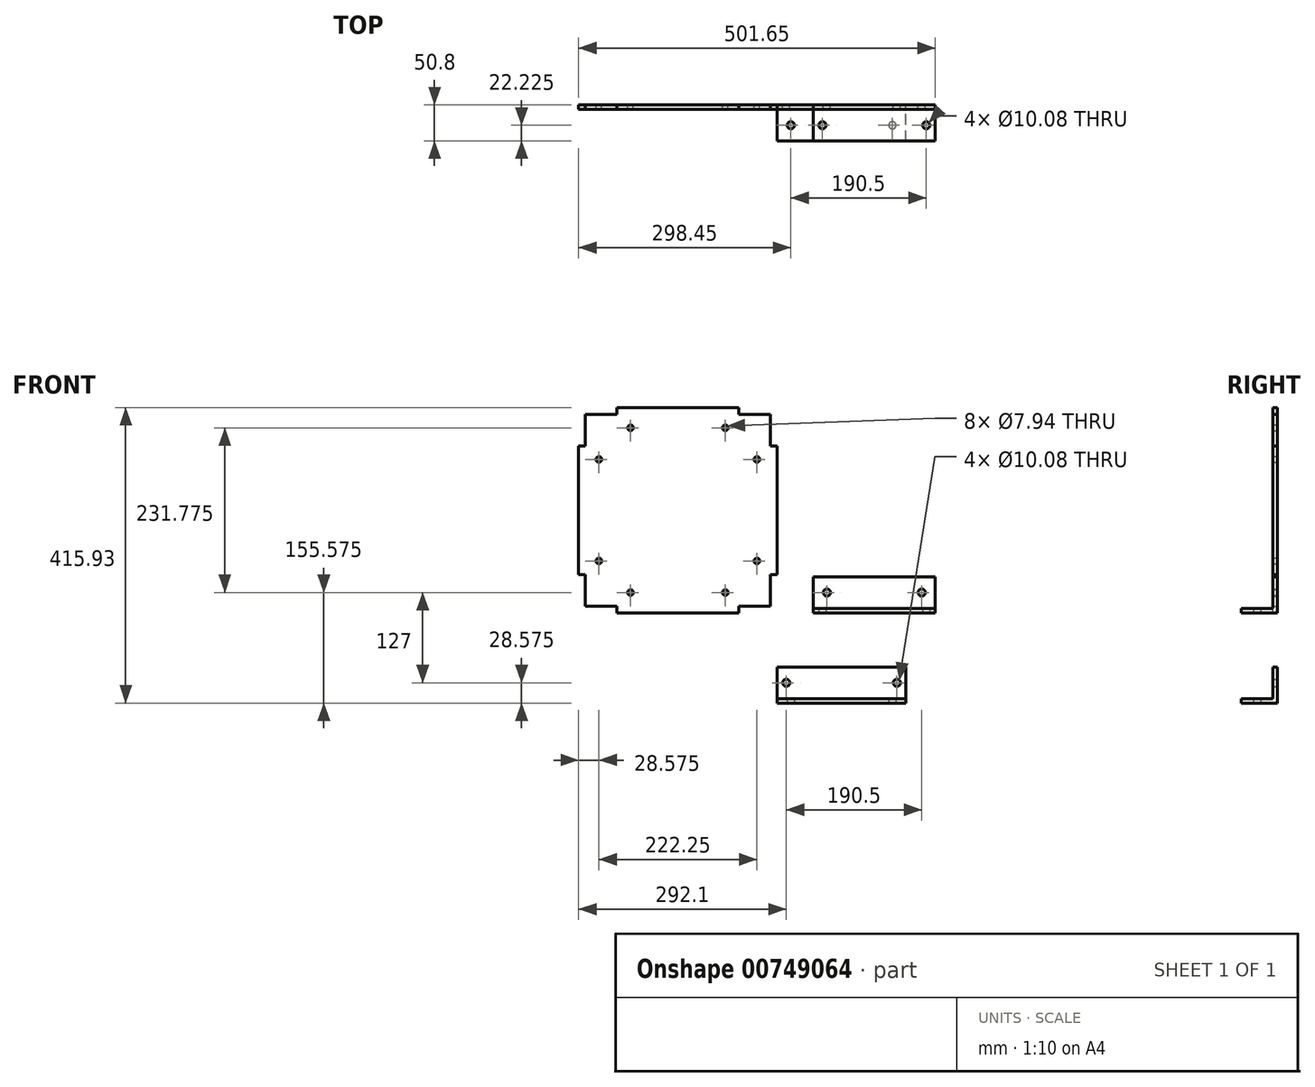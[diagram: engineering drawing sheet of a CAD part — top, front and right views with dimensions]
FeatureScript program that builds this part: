
annotation { "Feature Type Name" : "Feature", "Feature Type Description" : "" }
export const myFeature = defineFeature(function(context is Context, id is Id, definition is map)
    precondition{}
    {
        {
            var Q0;
            Q0=qCreatedBy(makeId("Front.planeOp"),FACE);
            var sketch = newSketch(context, id + "F0", { "sketchPlane" : qUnion([Q0])});
            skLineSegment(sketch, "E0.bottom", {"start": v(-53.98, 0) * mm, "end": v(-225.42, 0) * mm});
            skLineSegment(sketch, "E0.top", {"start": v(-53.98, 288.93) * mm, "end": v(-225.42, 288.93) * mm});
            skLineSegment(sketch, "E0.left", {"start": v(0, 53.98) * mm, "end": v(0, 234.95) * mm});
            skLineSegment(sketch, "E0.right", {"start": v(-279.4, 53.97) * mm, "end": v(-279.4, 234.95) * mm});
            skLineSegment(sketch, "E1", {"start": v(-139.7, 288.93) * mm, "end": v(-139.7, 0) * mm, "construction": true});
            skLineSegment(sketch, "E2", {"start": v(-279.4, 144.46) * mm, "end": v(0, 144.46) * mm, "construction": true});
            skLineSegment(sketch, "E3.top", {"start": v(-279.4, 234.95) * mm, "end": v(-269.88, 234.95) * mm});
            skLineSegment(sketch, "E3.right", {"start": v(-269.88, 279.4) * mm, "end": v(-269.88, 234.95) * mm});
            skLineSegment(sketch, "E4.top", {"start": v(-225.42, 279.4) * mm, "end": v(-269.88, 279.4) * mm});
            skLineSegment(sketch, "E4.left", {"start": v(-225.42, 288.93) * mm, "end": v(-225.42, 279.4) * mm});
            skPoint(sketch, "E5.orphan", {"position": v(-279.4, 288.93) * mm});
            skLineSegment(sketch, "E6.MirrorCS", {"start": v(-53.98, 288.93) * mm, "end": v(-53.98, 279.4) * mm});
            skLineSegment(sketch, "E7.MirrorCS", {"start": v(-53.98, 279.4) * mm, "end": v(-9.53, 279.4) * mm});
            skLineSegment(sketch, "E8.MirrorCS", {"start": v(-9.53, 279.4) * mm, "end": v(-9.53, 234.95) * mm});
            skLineSegment(sketch, "E9.MirrorCS", {"start": v(0, 234.95) * mm, "end": v(-9.53, 234.95) * mm});
            skLineSegment(sketch, "E10.MirrorCS", {"start": v(-53.98, 9.53) * mm, "end": v(-9.53, 9.53) * mm});
            skLineSegment(sketch, "E11.MirrorCS", {"start": v(-53.98, 0) * mm, "end": v(-53.98, 9.53) * mm});
            skLineSegment(sketch, "E12.MirrorCS", {"start": v(0, 53.97) * mm, "end": v(-9.53, 53.97) * mm});
            skLineSegment(sketch, "E13.MirrorCS", {"start": v(-9.53, 9.53) * mm, "end": v(-9.53, 53.97) * mm});
            skLineSegment(sketch, "E14.MirrorCS", {"start": v(-279.4, 53.97) * mm, "end": v(-269.88, 53.97) * mm});
            skLineSegment(sketch, "E15.MirrorCS", {"start": v(-269.88, 9.53) * mm, "end": v(-269.88, 53.97) * mm});
            skLineSegment(sketch, "E16.MirrorCS", {"start": v(-225.42, 9.53) * mm, "end": v(-269.88, 9.53) * mm});
            skLineSegment(sketch, "E17.MirrorCS", {"start": v(-225.42, 0) * mm, "end": v(-225.42, 9.53) * mm});
            skPoint(sketch, "E18.orphan", {"position": v(-279.4, 0) * mm});
            skPoint(sketch, "E19.orphan", {"position": v(0, 0) * mm});
            skPoint(sketch, "E20.orphan", {"position": v(0, 288.92) * mm});
            skSolve(sketch);
        }
        {
            var Q0;
            Q0 = qSketchRegion(id + "F0", true);
            extrude(context, id + "F1", {"entities" : qUnion([Q0]), "depth" : 6.35 * mm, "offsetDistance" : 25.4 * mm});
        }
        {
            var Q0;
            Q0=makeQuery(id+"F1.opExtrude","CAP_FACE",FACE,{"disambiguationData":[OSD([sQuery(id+"F0.wireOp",EDGE,"E0.bottom"),sQuery(id+"F0.wireOp",EDGE,"E0.top"),sQuery(id+"F0.wireOp",EDGE,"E0.left"),sQuery(id+"F0.wireOp",EDGE,"E0.right"),sQuery(id+"F0.wireOp",EDGE,"E3.top"),sQuery(id+"F0.wireOp",EDGE,"E3.right"),sQuery(id+"F0.wireOp",EDGE,"E4.top"),sQuery(id+"F0.wireOp",EDGE,"E4.left"),sQuery(id+"F0.wireOp",EDGE,"E6.MirrorCS"),sQuery(id+"F0.wireOp",EDGE,"E7.MirrorCS"),sQuery(id+"F0.wireOp",EDGE,"E8.MirrorCS"),sQuery(id+"F0.wireOp",EDGE,"E9.MirrorCS"),sQuery(id+"F0.wireOp",EDGE,"E10.MirrorCS"),sQuery(id+"F0.wireOp",EDGE,"E11.MirrorCS"),sQuery(id+"F0.wireOp",EDGE,"E12.MirrorCS"),sQuery(id+"F0.wireOp",EDGE,"E13.MirrorCS"),sQuery(id+"F0.wireOp",EDGE,"E14.MirrorCS"),sQuery(id+"F0.wireOp",EDGE,"E15.MirrorCS"),sQuery(id+"F0.wireOp",EDGE,"E16.MirrorCS"),sQuery(id+"F0.wireOp",EDGE,"E17.MirrorCS")])],"isStart":false});
            var sketch = newSketch(context, id + "F2", { "sketchPlane" : qUnion([Q0])});
            skLineSegment(sketch, "E21", {"start": v(-9.53, 28.58) * mm, "end": v(-269.88, 28.58) * mm, "construction": true});
            skLineSegment(sketch, "E22", {"start": v(-139.7, 0) * mm, "end": v(-139.7, 288.93) * mm, "construction": true});
            skLineSegment(sketch, "E23", {"start": v(0, 144.46) * mm, "end": v(-279.4, 144.46) * mm, "construction": true});
            skPoint(sketch, "E24", {"position": v(-73.03, 28.58) * mm});
            skLineSegment(sketch, "E25", {"start": v(-28.58, 28.58) * mm, "end": v(-28.58, 279.4) * mm, "construction": true});
            skPoint(sketch, "E26", {"position": v(-28.57, 73.03) * mm});
            skPoint(sketch, "E27.MirrorP", {"position": v(-206.38, 28.57) * mm});
            skPoint(sketch, "E28.MirrorP", {"position": v(-250.83, 73.02) * mm});
            skPoint(sketch, "E29.MirrorP", {"position": v(-250.83, 215.9) * mm});
            skPoint(sketch, "E30.MirrorP", {"position": v(-206.38, 260.35) * mm});
            skPoint(sketch, "E31.MirrorP", {"position": v(-73.03, 260.35) * mm});
            skPoint(sketch, "E32.MirrorP", {"position": v(-28.58, 215.9) * mm});
            skSolve(sketch);
        }
        {
            var Q0;
            Q0=sQuery(id+"F2.wireOp",VERTEX,"E26");
            var Q1;
            Q1=sQuery(id+"F2.wireOp",VERTEX,"E24");
            var Q2;
            Q2=sQuery(id+"F2.wireOp",VERTEX,"E28.MirrorP");
            var Q3;
            Q3=sQuery(id+"F2.wireOp",VERTEX,"E27.MirrorP");
            var Q4;
            Q4=sQuery(id+"F2.wireOp",VERTEX,"E29.MirrorP");
            var Q5;
            Q5=sQuery(id+"F2.wireOp",VERTEX,"E30.MirrorP");
            var Q6;
            Q6=sQuery(id+"F2.wireOp",VERTEX,"E31.MirrorP");
            var Q7;
            Q7=sQuery(id+"F2.wireOp",VERTEX,"E32.MirrorP");
            var Q8;
            Q8=makeQuery(id+"F1.opExtrude","SWEPT_BODY",BODY,{"disambiguationData":[OSD([sQuery(id+"F0.wireOp",EDGE,"E0.bottom"),sQuery(id+"F0.wireOp",EDGE,"E0.top"),sQuery(id+"F0.wireOp",EDGE,"E0.left"),sQuery(id+"F0.wireOp",EDGE,"E0.right"),sQuery(id+"F0.wireOp",EDGE,"E3.top"),sQuery(id+"F0.wireOp",EDGE,"E3.right"),sQuery(id+"F0.wireOp",EDGE,"E4.top"),sQuery(id+"F0.wireOp",EDGE,"E4.left"),sQuery(id+"F0.wireOp",EDGE,"E6.MirrorCS"),sQuery(id+"F0.wireOp",EDGE,"E7.MirrorCS"),sQuery(id+"F0.wireOp",EDGE,"E8.MirrorCS"),sQuery(id+"F0.wireOp",EDGE,"E9.MirrorCS"),sQuery(id+"F0.wireOp",EDGE,"E10.MirrorCS"),sQuery(id+"F0.wireOp",EDGE,"E11.MirrorCS"),sQuery(id+"F0.wireOp",EDGE,"E12.MirrorCS"),sQuery(id+"F0.wireOp",EDGE,"E13.MirrorCS"),sQuery(id+"F0.wireOp",EDGE,"E14.MirrorCS"),sQuery(id+"F0.wireOp",EDGE,"E15.MirrorCS"),sQuery(id+"F0.wireOp",EDGE,"E16.MirrorCS"),sQuery(id+"F0.wireOp",EDGE,"E17.MirrorCS")])]});
            hole(context, id + "F3", {"style" : HoleStyle.SIMPLE, "endStyle" : HoleEndStyle.BLIND, "standardTappedOrClearance" : lookupTablePath({ "standard" : "ANSI", "engagement" : "75%", "pitch" : "16 tpi", "size" : "3/8", "type" : "Tapped" }), "standardBlindInLast" : lookupTablePath({ "standard" : "ANSI", "engagement" : "75%", "pitch" : "16 tpi", "size" : "3/8", "type" : "Tapped" }), "holeDiameter" : 7.94 * mm, "majorDiameter" : 9.52 * mm, "showTappedDepth" : true, "holeDepth" : 20.68 * mm, "isTappedThrough" : true, "tappedDepth" : 15.9 * mm, "tapClearance" : 3, "locations" : qUnion([Q0, Q1, Q2, Q3, Q4, Q5, Q6, Q7]), "scope" : qUnion([Q8])});
        }
        {
            var Q0;
            Q0=qCreatedBy(makeId("Front.planeOp"),FACE);
            var sketch = newSketch(context, id + "F4", { "sketchPlane" : qUnion([Q0])});
            skLineSegment(sketch, "E33.bottom", {"start": v(50.8, 0) * mm, "end": v(222.25, 0) * mm});
            skLineSegment(sketch, "E33.top", {"start": v(50.8, 50.8) * mm, "end": v(222.25, 50.8) * mm});
            skLineSegment(sketch, "E33.left", {"start": v(50.8, 0) * mm, "end": v(50.8, 50.8) * mm});
            skLineSegment(sketch, "E33.right", {"start": v(222.25, 0) * mm, "end": v(222.25, 50.8) * mm});
            skSolve(sketch);
        }
        {
            var Q0;
            Q0 = qSketchRegion(id + "F4", true);
            extrude(context, id + "F5", {"entities" : qUnion([Q0]), "depth" : 50.8 * mm, "offsetDistance" : 25.4 * mm});
        }
        {
            var Q0;
            Q0=makeQuery(id+"F5.opExtrude","SWEPT_FACE",FACE,{"disambiguationData":[OSD([sQuery(id+"F4.wireOp",EDGE,"E33.right")])]});
            var sketch = newSketch(context, id + "F6", { "sketchPlane" : qUnion([Q0])});
            skLineSegment(sketch, "E34.bottom", {"start": v(-50.8, 50.8) * mm, "end": v(-6.35, 50.8) * mm});
            skLineSegment(sketch, "E34.top", {"start": v(-50.8, 6.35) * mm, "end": v(-6.35, 6.35) * mm});
            skLineSegment(sketch, "E34.left", {"start": v(-50.8, 50.8) * mm, "end": v(-50.8, 6.35) * mm});
            skLineSegment(sketch, "E34.right", {"start": v(-6.35, 50.8) * mm, "end": v(-6.35, 6.35) * mm});
            skSolve(sketch);
        }
        {
            var Q0;
            Q0 = qSketchRegion(id + "F6", true);
            extrude(context, id + "F7", {"entities" : qUnion([Q0]), "operationType" : NewBodyOperationType.REMOVE, "oppositeDirection" : true, "depth" : 171.45 * mm, "offsetDistance" : 25.4 * mm});
        }
        {
            var Q0;
            Q0=makeQuery(id+"F7.boolean.opBoolean","COPY",FACE,{"derivedFrom":makeQuery(id+"F7.opExtrude","SWEPT_FACE",FACE,{"disambiguationData":[OSD([sQuery(id+"F6.wireOp",EDGE,"E34.top")])]})});
            var sketch = newSketch(context, id + "F8", { "sketchPlane" : qUnion([Q0])});
            skLineSegment(sketch, "E35", {"start": v(50.8, -28.57) * mm, "end": v(222.25, -28.57) * mm, "construction": true});
            skLineSegment(sketch, "E36", {"start": v(136.53, -50.8) * mm, "end": v(136.53, -6.35) * mm, "construction": true});
            skPoint(sketch, "E37", {"position": v(63.5, -28.57) * mm});
            skPoint(sketch, "E38.MirrorP", {"position": v(209.55, -28.57) * mm});
            skSolve(sketch);
        }
        {
            var Q0;
            Q0=makeQuery(id+"F7.boolean.opBoolean","COPY",FACE,{"derivedFrom":makeQuery(id+"F7.opExtrude","SWEPT_FACE",FACE,{"disambiguationData":[OSD([sQuery(id+"F6.wireOp",EDGE,"E34.right")])]})});
            var sketch = newSketch(context, id + "F9", { "sketchPlane" : qUnion([Q0])});
            skLineSegment(sketch, "E39", {"start": v(50.8, 28.57) * mm, "end": v(222.25, 28.58) * mm, "construction": true});
            skLineSegment(sketch, "E40", {"start": v(136.53, 28.57) * mm, "end": v(136.53, 50.8) * mm, "construction": true});
            skPoint(sketch, "E41", {"position": v(69.85, 28.57) * mm});
            skPoint(sketch, "E42.MirrorP", {"position": v(203.2, 28.57) * mm});
            skSolve(sketch);
        }
        {
            var Q0;
            Q0=sQuery(id+"F9.wireOp",VERTEX,"E41");
            var Q1;
            Q1=sQuery(id+"F9.wireOp",VERTEX,"E42.MirrorP");
            var Q2;
            Q2=sQuery(id+"F8.wireOp",VERTEX,"E37");
            var Q3;
            Q3=sQuery(id+"F8.wireOp",VERTEX,"E38.MirrorP");
            var Q4;
            Q4=makeQuery(id+"F5.opExtrude","SWEPT_BODY",BODY,{"disambiguationData":[OSD([sQuery(id+"F4.wireOp",EDGE,"E33.bottom"),sQuery(id+"F4.wireOp",EDGE,"E33.top"),sQuery(id+"F4.wireOp",EDGE,"E33.left"),sQuery(id+"F4.wireOp",EDGE,"E33.right")])]});
            hole(context, id + "F10", {"style" : HoleStyle.SIMPLE, "endStyle" : HoleEndStyle.BLIND, "standardTappedOrClearance" : lookupTablePath({ "standard" : "ANSI", "fit" : "Normal (ASME)", "size" : "3/8", "type" : "Clearance" }), "standardBlindInLast" : lookupTablePath({ "fit" : "Free", "standard" : "ANSI", "size" : "3/8", "type" : "Clearance" }), "holeDiameter" : 10.08 * mm, "majorDiameter" : 9.52 * mm, "holeDepth" : 20.68 * mm, "isTappedThrough" : true, "tappedDepth" : 15.9 * mm, "tapClearance" : 3, "locations" : qUnion([Q0, Q1, Q2, Q3]), "scope" : qUnion([Q4])});
        }
        {
            var Q0;
            Q0=qCreatedBy(makeId("Front.planeOp"),FACE);
            var sketch = newSketch(context, id + "F11", { "sketchPlane" : qUnion([Q0])});
            skLineSegment(sketch, "E43.bottom", {"start": v(0, -76.2) * mm, "end": v(180.98, -76.2) * mm});
            skLineSegment(sketch, "E43.top", {"start": v(0, -127) * mm, "end": v(180.98, -127) * mm});
            skLineSegment(sketch, "E43.left", {"start": v(0, -76.2) * mm, "end": v(0, -127) * mm});
            skLineSegment(sketch, "E43.right", {"start": v(180.98, -76.2) * mm, "end": v(180.98, -127) * mm});
            skSolve(sketch);
        }
        {
            var Q0;
            Q0 = qSketchRegion(id + "F11", true);
            extrude(context, id + "F12", {"entities" : qUnion([Q0]), "depth" : 50.8 * mm, "offsetDistance" : 25.4 * mm});
        }
        {
            var Q0;
            Q0=makeQuery(id+"F12.opExtrude","SWEPT_FACE",FACE,{"disambiguationData":[OSD([sQuery(id+"F11.wireOp",EDGE,"E43.right")])]});
            var sketch = newSketch(context, id + "F13", { "sketchPlane" : qUnion([Q0])});
            skLineSegment(sketch, "E44.bottom", {"start": v(-50.8, -76.2) * mm, "end": v(-6.35, -76.2) * mm});
            skLineSegment(sketch, "E44.top", {"start": v(-50.8, -120.65) * mm, "end": v(-6.35, -120.65) * mm});
            skLineSegment(sketch, "E44.left", {"start": v(-50.8, -76.2) * mm, "end": v(-50.8, -120.65) * mm});
            skLineSegment(sketch, "E44.right", {"start": v(-6.35, -76.2) * mm, "end": v(-6.35, -120.65) * mm});
            skSolve(sketch);
        }
        {
            var Q0;
            Q0 = qSketchRegion(id + "F13", true);
            extrude(context, id + "F14", {"entities" : qUnion([Q0]), "operationType" : NewBodyOperationType.REMOVE, "oppositeDirection" : true, "depth" : 180.97 * mm, "offsetDistance" : 25.4 * mm});
        }
        {
            var Q0;
            Q0=makeQuery(id+"F14.boolean.opBoolean","COPY",FACE,{"derivedFrom":makeQuery(id+"F14.opExtrude","SWEPT_FACE",FACE,{"disambiguationData":[OSD([sQuery(id+"F13.wireOp",EDGE,"E44.right")])]})});
            var sketch = newSketch(context, id + "F15", { "sketchPlane" : qUnion([Q0])});
            skLineSegment(sketch, "E45", {"start": v(0, -98.43) * mm, "end": v(180.98, -98.43) * mm, "construction": true});
            skLineSegment(sketch, "E46", {"start": v(90.49, -98.43) * mm, "end": v(90.49, -76.2) * mm, "construction": true});
            skPoint(sketch, "E47", {"position": v(12.7, -98.43) * mm});
            skPoint(sketch, "E48.MirrorP", {"position": v(168.28, -98.43) * mm});
            skSolve(sketch);
        }
        {
            var Q0;
            Q0=makeQuery(id+"F14.boolean.opBoolean","COPY",FACE,{"derivedFrom":makeQuery(id+"F14.opExtrude","SWEPT_FACE",FACE,{"disambiguationData":[OSD([sQuery(id+"F13.wireOp",EDGE,"E44.top")])]})});
            var sketch = newSketch(context, id + "F16", { "sketchPlane" : qUnion([Q0])});
            skLineSegment(sketch, "E49", {"start": v(0, -28.58) * mm, "end": v(180.98, -28.58) * mm, "construction": true});
            skLineSegment(sketch, "E50", {"start": v(90.49, -28.58) * mm, "end": v(90.49, -6.35) * mm, "construction": true});
            skPoint(sketch, "E51", {"position": v(19.05, -28.58) * mm});
            skPoint(sketch, "E52.MirrorP", {"position": v(161.93, -28.58) * mm});
            skSolve(sketch);
        }
        {
            var Q0;
            Q0=sQuery(id+"F15.wireOp",VERTEX,"E47");
            var Q1;
            Q1=sQuery(id+"F15.wireOp",VERTEX,"E48.MirrorP");
            var Q2;
            Q2=sQuery(id+"F16.wireOp",VERTEX,"E51");
            var Q3;
            Q3=sQuery(id+"F16.wireOp",VERTEX,"E52.MirrorP");
            var Q4;
            Q4=makeQuery(id+"F12.opExtrude","SWEPT_BODY",BODY,{"disambiguationData":[OSD([sQuery(id+"F11.wireOp",EDGE,"E43.bottom"),sQuery(id+"F11.wireOp",EDGE,"E43.top"),sQuery(id+"F11.wireOp",EDGE,"E43.left"),sQuery(id+"F11.wireOp",EDGE,"E43.right")])]});
            hole(context, id + "F17", {"style" : HoleStyle.SIMPLE, "endStyle" : HoleEndStyle.BLIND, "standardTappedOrClearance" : lookupTablePath({ "standard" : "ANSI", "fit" : "Normal (ASME)", "size" : "3/8", "type" : "Clearance" }), "standardBlindInLast" : lookupTablePath({ "fit" : "Free", "standard" : "ANSI", "size" : "3/8", "type" : "Clearance" }), "holeDiameter" : 10.08 * mm, "majorDiameter" : 6.35 * mm, "holeDepth" : 20.68 * mm, "isTappedThrough" : true, "tappedDepth" : 15.93 * mm, "tapClearance" : 3, "locations" : qUnion([Q0, Q1, Q2, Q3]), "scope" : qUnion([Q4])});
        }
    });
